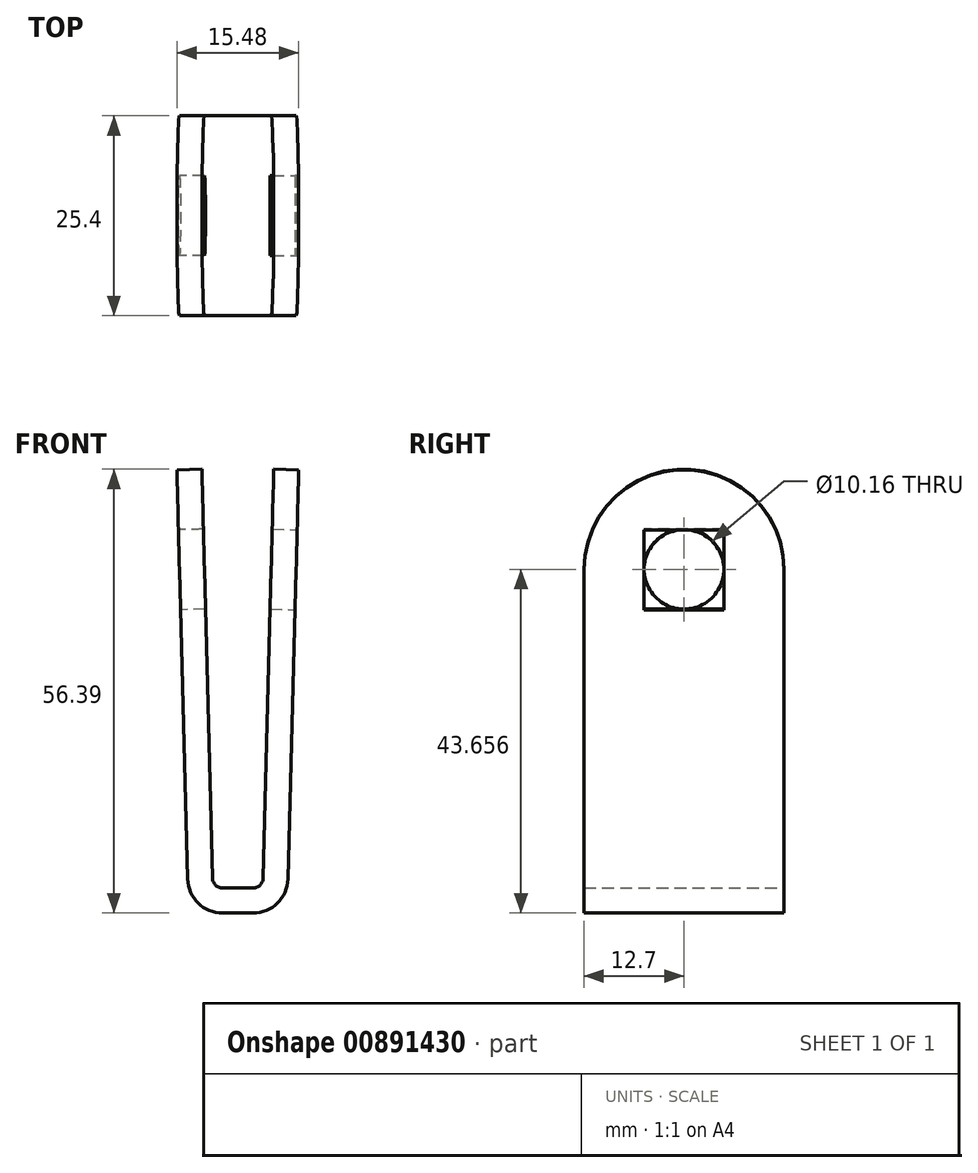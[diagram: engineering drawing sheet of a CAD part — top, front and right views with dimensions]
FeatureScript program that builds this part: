
annotation { "Feature Type Name" : "Feature", "Feature Type Description" : "" }
export const myFeature = defineFeature(function(context is Context, id is Id, definition is map)
    precondition{}
    {
        {
            var Q0;
            Q0=qCreatedBy(makeId("Front.planeOp"),FACE);
            var sketch = newSketch(context, id + "F0", { "sketchPlane" : qUnion([Q0])});
            skLineSegment(sketch, "E0", {"start": v(-3.17, 0) * mm, "end": v(3.18, 0) * mm});
            skLineSegment(sketch, "E1", {"start": v(3.17, 0) * mm, "end": v(4.57, 53.21) * mm});
            skLineSegment(sketch, "E2", {"start": v(4.57, 53.21) * mm, "end": v(7.74, 53.13) * mm});
            skLineSegment(sketch, "E3", {"start": v(7.74, 53.13) * mm, "end": v(6.27, -3.18) * mm});
            skLineSegment(sketch, "E4", {"start": v(6.27, -3.18) * mm, "end": v(-6.27, -3.18) * mm});
            skLineSegment(sketch, "E5", {"start": v(-6.27, -3.18) * mm, "end": v(-7.74, 53.13) * mm});
            skLineSegment(sketch, "E6", {"start": v(-7.74, 53.13) * mm, "end": v(-4.57, 53.21) * mm});
            skLineSegment(sketch, "E7", {"start": v(-4.57, 53.21) * mm, "end": v(-3.17, 0) * mm});
            skLineSegment(sketch, "E8", {"start": v(-4.57, 53.21) * mm, "end": v(4.57, 53.21) * mm, "construction": true});
            skSolve(sketch);
        }
        {
            var Q0;
            Q0 = qSketchRegion(id + "F0", true);
            extrude(context, id + "F1", {"entities" : qUnion([Q0]), "depth" : 12.7 * mm, "offsetDistance" : 25.4 * mm, "hasSecondDirection" : true, "secondDirectionOppositeDirection" : true, "secondDirectionDepth" : 12.7 * mm});
        }
        {
            var Q0;
            Q0=makeQuery(id+"F1.opExtrude","SWEPT_FACE",FACE,{"disambiguationData":[OSD([sQuery(id+"F0.wireOp",EDGE,"E3")])]});
            var sketch = newSketch(context, id + "F2", { "sketchPlane" : qUnion([Q0])});
            skLineSegment(sketch, "E9.0", {"start": v(-12.7, 53.31) * mm, "end": v(-12.7, -3) * mm, "construction": true});
            skLineSegment(sketch, "E10.0", {"start": v(12.7, 53.31) * mm, "end": v(12.7, -3) * mm, "construction": true});
            skLineSegment(sketch, "E11.0", {"start": v(-12.7, 53.31) * mm, "end": v(12.7, 53.31) * mm, "construction": true});
            skArc(sketch, "E12", {"start": v(12.7, 40.61) * mm, "mid": v(0, 53.31) * mm, "end": v(-12.7, 40.61) * mm});
            skPoint(sketch, "E13", {"position": v(0, 53.31) * mm});
            skLineSegment(sketch, "E14", {"start": v(-12.7, 40.61) * mm, "end": v(-12.7, 53.31) * mm});
            skLineSegment(sketch, "E15", {"start": v(12.7, 53.31) * mm, "end": v(-12.7, 53.31) * mm});
            skLineSegment(sketch, "E16", {"start": v(12.7, 53.31) * mm, "end": v(12.7, 40.61) * mm});
            skLineSegment(sketch, "E17.bottom", {"start": v(5.08, 45.7) * mm, "end": v(-5.08, 45.7) * mm});
            skLineSegment(sketch, "E17.top", {"start": v(5.08, 35.53) * mm, "end": v(-5.08, 35.53) * mm});
            skLineSegment(sketch, "E17.left", {"start": v(5.08, 45.7) * mm, "end": v(5.08, 35.53) * mm});
            skLineSegment(sketch, "E17.right", {"start": v(-5.08, 45.7) * mm, "end": v(-5.08, 35.53) * mm});
            skSolve(sketch);
        }
        {
            var Q0;
            {var subQ0=sQuery(id+"F2.wireOp",EDGE,"E14");Q0=makeQuery(id+"F2.imprint","IMPRINT",FACE,{"disambiguationData":[TD([[makeQuery(id+"F2.imprint","IMPRINT",EDGE,{"derivedFrom":subQ0}),1.0]])]});}
            var Q1;
            {var subQ0=sQuery(id+"F2.wireOp",EDGE,"E16");Q1=makeQuery(id+"F2.imprint","IMPRINT",FACE,{"disambiguationData":[TD([[makeQuery(id+"F2.imprint","IMPRINT",EDGE,{"derivedFrom":subQ0}),-1.0]])]});}
            var Q2;
            Q2=makeQuery(id+"F2.imprint","IMPRINT",FACE,{"disambiguationData":[TD([[makeQuery(id+"F2.imprint","IMPRINT",EDGE,{"derivedFrom":sQuery(id+"F2.wireOp",EDGE,"E17.bottom")}),1.0]])]});
            var Q3;
            Q3=makeQuery(id+"F1.opExtrude","SWEPT_FACE",FACE,{"disambiguationData":[OSD([sQuery(id+"F0.wireOp",EDGE,"E1")])]});
            extrude(context, id + "F3", {"entities" : qUnion([Q0, Q1, Q2]), "operationType" : NewBodyOperationType.REMOVE, "endBound" : BoundingType.UP_TO_SURFACE, "oppositeDirection" : true, "depth" : 25.4 * mm, "endBoundEntityFace" : qUnion([Q3]), "offsetDistance" : 25.4 * mm});
        }
        {
            var Q0;
            Q0=makeQuery(id+"F1.opExtrude","SWEPT_FACE",FACE,{"disambiguationData":[OSD([sQuery(id+"F0.wireOp",EDGE,"E5")])]});
            var sketch = newSketch(context, id + "F4", { "sketchPlane" : qUnion([Q0])});
            skLineSegment(sketch, "E18.0", {"start": v(-12.7, -3) * mm, "end": v(-12.7, 53.31) * mm, "construction": true});
            skLineSegment(sketch, "E19.0", {"start": v(12.7, -3) * mm, "end": v(12.7, 53.31) * mm, "construction": true});
            skLineSegment(sketch, "E20.0", {"start": v(12.7, 53.31) * mm, "end": v(-12.7, 53.31) * mm, "construction": true});
            skArc(sketch, "E21", {"start": v(12.7, 40.61) * mm, "mid": v(0, 53.31) * mm, "end": v(-12.7, 40.61) * mm});
            skPoint(sketch, "E22", {"position": v(0, 53.31) * mm});
            skLineSegment(sketch, "E23", {"start": v(-12.7, 40.61) * mm, "end": v(-12.7, 53.31) * mm});
            skLineSegment(sketch, "E24", {"start": v(12.7, 53.31) * mm, "end": v(-12.7, 53.31) * mm});
            skLineSegment(sketch, "E25", {"start": v(12.7, 53.31) * mm, "end": v(12.7, 40.61) * mm});
            skSolve(sketch);
        }
        {
            var Q0;
            {var subQ0=sQuery(id+"F4.wireOp",EDGE,"E23");Q0=makeQuery(id+"F4.imprint","IMPRINT",FACE,{"disambiguationData":[TD([[makeQuery(id+"F4.imprint","IMPRINT",EDGE,{"derivedFrom":subQ0}),-1.0]])]});}
            var Q1;
            {var subQ0=sQuery(id+"F4.wireOp",EDGE,"E25");Q1=makeQuery(id+"F4.imprint","IMPRINT",FACE,{"disambiguationData":[TD([[makeQuery(id+"F4.imprint","IMPRINT",EDGE,{"derivedFrom":subQ0}),1.0]])]});}
            var Q2;
            Q2=makeQuery(id+"F1.opExtrude","SWEPT_FACE",FACE,{"disambiguationData":[OSD([sQuery(id+"F0.wireOp",EDGE,"E7")])]});
            extrude(context, id + "F5", {"entities" : qUnion([Q0, Q1]), "operationType" : NewBodyOperationType.REMOVE, "endBound" : BoundingType.UP_TO_SURFACE, "oppositeDirection" : true, "depth" : 25.4 * mm, "endBoundEntityFace" : qUnion([Q2]), "offsetDistance" : 25.4 * mm});
        }
        {
            var Q0;
            Q0=makeQuery(id+"F1.opExtrude","SWEPT_EDGE",EDGE,{"disambiguationData":[OSD([sQuery(id+"F0.wireOp",EDGE,"E0"),sQuery(id+"F0.wireOp",EDGE,"E1")])]});
            var Q1;
            Q1=makeQuery(id+"F1.opExtrude","SWEPT_EDGE",EDGE,{"disambiguationData":[OSD([sQuery(id+"F0.wireOp",EDGE,"E0"),sQuery(id+"F0.wireOp",EDGE,"E7")])]});
            fillet(context, id + "F6", {"entities" : qUnion([Q0, Q1]), "radius" : 1.27 * mm, "tangentPropagation" : true, "allowEdgeOverflow" : false});
        }
        {
            var Q0;
            Q0=makeQuery(id+"F1.opExtrude","SWEPT_EDGE",EDGE,{"disambiguationData":[OSD([sQuery(id+"F0.wireOp",EDGE,"E3"),sQuery(id+"F0.wireOp",EDGE,"E4")])]});
            var Q1;
            Q1=makeQuery(id+"F1.opExtrude","SWEPT_EDGE",EDGE,{"disambiguationData":[OSD([sQuery(id+"F0.wireOp",EDGE,"E4"),sQuery(id+"F0.wireOp",EDGE,"E5")])]});
            fillet(context, id + "F7", {"entities" : qUnion([Q0, Q1]), "radius" : 4.44 * mm, "tangentPropagation" : true, "allowEdgeOverflow" : false});
        }
        {
            var Q0;
            Q0=sQuery(id+"F4.wireOp",VERTEX,"E21.center");
            var Q1;
            Q1=makeQuery(id+"F1.opExtrude","SWEPT_BODY",BODY,{"disambiguationData":[OSD([sQuery(id+"F0.wireOp",EDGE,"E0"),sQuery(id+"F0.wireOp",EDGE,"E1"),sQuery(id+"F0.wireOp",EDGE,"E2"),sQuery(id+"F0.wireOp",EDGE,"E3"),sQuery(id+"F0.wireOp",EDGE,"E4"),sQuery(id+"F0.wireOp",EDGE,"E5"),sQuery(id+"F0.wireOp",EDGE,"E6"),sQuery(id+"F0.wireOp",EDGE,"E7")])]});
            hole(context, id + "F8", {"style" : HoleStyle.SIMPLE, "endStyle" : HoleEndStyle.BLIND, "holeDiameter" : 10.16 * mm, "majorDiameter" : 6.35 * mm, "holeDepth" : 3.17 * mm, "isTappedThrough" : true, "tappedDepth" : 12.7 * mm, "tapClearance" : 3, "startFromSketch" : true, "locations" : qUnion([Q0]), "scope" : qUnion([Q1])});
        }
    });
